# Revit family: Residential_Boiler-Lochinvar-Knight-KHB_Series
name_source: partatom
category: Mechanical Equipment
revit_build: Autodesk Revit 2014 (Build: 20130308_1515(x64)
units: mm (PartAtom-declared; Revit-internal decimal feet)

## types (12) — shared parameters
ASME Tank Construction = Yes
Assembly Code = D3020100
Default Elevation = 0"
Description = Knight Fire Tube Boiler
Drain Connection Diameter = 3/4"
Frequency = 60 Hz
Gas Connection Description = Gas Supply Connection 1/2"
Gas Supply Connection Diameter = 1/2"
Height = 43 3/8"
Hot Water Connection Diameter = 1"
I = 15"
K = 8 11/32"
Leg Width = 17"
Length = 19"
Manufacturer = Lochinvar
Material = Metal-Lochinvar-Steel
Phase = 1
Price = Prices may vary. Please consult Manufacturer Representative for most up-to-date price list.
Product Documentation Link = http://www.lochinvar.com
Product Page URL = http://www.lochinvar.com
URL = http://www.lochinvar.com
Voltage = 120 V
Warranty Information = 15-Year Limited Warranty, 5-Year Limited Parts Warranty
Width = 16"

## per-type parameters (varying)
| type | A | Air Intake Connection Description | Air Intake Connection Diameter | B | C | Cold Water Connection Description | Cold Water Connection Diameter | D | E | Exhaust Air Connection Description | Exhaust Air Connection Diameter | F | Fuel Type | G | H | Hood Width | Hot Water Connection Description | J | Shipping Weight | Total Heating Capacity | Venting Diameter |
| KHB055N | 3 1/2" | Air Intake Connection 2" | 2" | 13 1/4" | 6" | Cold Water Connection Inlet 1" NPT | 1" | 2 3/4" | 37 21/32" | Exhaust Air Connection 2" | 2" | 13 1/2" | Natural Gas | 8 11/32" | 10 1/2" | 3 1/2" | Hot Water Connection Outlet 1" NPT | 32 1/2" | 160 lb | 55000.0 Btu/h | 2" |
| KHB085N | 3 1/2" | Air Intake Connection 2" | 2" | 13 1/4" | 6" | Cold Water Connection Inlet 1" NPT | 1" | 2 3/4" | 37 21/32" | Exhaust Air Connection 2" | 2" | 13 1/2" | Natural Gas | 8 11/32" | 10 1/2" | 3 1/2" | Hot Water Connection Outlet 1" NPT | 32 1/2" | 170 lb | 85000.0 Btu/h | 2" |
| KHB110N | 2 3/4" | Air Intake Connection 3" | 3" | 14 3/4" | 7 1/2" | Cold Water Connection Inlet 1" NPT | 1" | 2 3/4" | 38" | Exhaust Air Connection 3" | 3" | 14 11/32" | Natural Gas | 9 3/4" | 10 1/2" | 2 3/4" | Hot Water Connection Outlet 1" NPT | 33" | 170 lb | 110000.0 Btu/h | 3" |
| KHB155N | 2 3/4" | Air Intake Connection 3" | 3" | 14 3/4" | 7 1/2" | Cold Water Connection Inlet 1" NPT | 1" | 2 1/2" | 38" | Exhaust Air Connection 3" | 3" | 14 11/32" | Natural Gas | 9 3/4" | 10 1/2" | 2 3/4" | Hot Water Connection Outlet 1" NPT | 33" | 180 lb | 155000.0 Btu/h | 3" |
| KHB199N | 3" | Air Intake Connection 3" | 3" | 15 1/2" | 7 1/2" | Cold Water Connection Inlet 1-1/4" NPT | 1 1/4" | 2 1/2" | 38 11/32" | Exhaust Air Connection 3" | 3" | 14 11/32" | Natural Gas | 10 1/2" | 11 1/2" | 3" | Hot Water Connection Outlet 1-1/4" NPT | 33" | 200 lb | 199999.0 Btu/h | 3" |
| KHB285N | 3" | Air Intake Connection 3" | 3" | 15 1/2" | 7 1/2" | Cold Water Connection Inlet 1-1/4" NPT | 1 1/4" | 2 1/2" | 38 11/32" | Exhaust Air Connection 3" | 3" | 14 11/32" | Natural Gas | 10 1/2" | 11 1/2" | 3" | Hot Water Connection Outlet 1-1/4" NPT | 33" | 210 lb | 285000.0 Btu/h | 3" |
| KHB285L | 3" | Air Intake Connection 3" | 3" | 15 1/2" | 7 1/2" | Cold Water Connection Inlet 1-1/4" NPT | 1 1/4" | 2 1/2" | 38 11/32" | Exhaust Air Connection 3" | 3" | 14 11/32" | LP Gas | 10 1/2" | 11 1/2" | 3" | Hot Water Connection Outlet 1-1/4" NPT | 33" | 210 lb | 285000.0 Btu/h | 3" |
| KHB055L | 3 1/2" | Air Intake Connection 2" | 2" | 13 1/4" | 6" | Cold Water Connection Inlet 1" NPT | 1" | 2 3/4" | 37 21/32" | Exhaust Air Connection 2" | 2" | 13 1/2" | LP Gas | 8 11/32" | 10 1/2" | 3 1/2" | Hot Water Connection Outlet 1" NPT | 32 1/2" | 160 lb | 55000.0 Btu/h | 2" |
| KHB085L | 3 1/2" | Air Intake Connection 2" | 2" | 13 1/4" | 6" | Cold Water Connection Inlet 1" NPT | 1" | 2 3/4" | 37 21/32" | Exhaust Air Connection 2" | 2" | 13 1/2" | LP Gas | 8 11/32" | 10 1/2" | 3 1/2" | Hot Water Connection Outlet 1" NPT | 32 1/2" | 170 lb | 85000.0 Btu/h | 2" |
| KHB110L | 2 3/4" | Air Intake Connection 3" | 3" | 14 3/4" | 7 1/2" | Cold Water Connection Inlet 1" NPT | 1" | 2 3/4" | 38" | Exhaust Air Connection 3" | 3" | 14 11/32" | LP Gas | 9 3/4" | 10 1/2" | 2 3/4" | Hot Water Connection Outlet 1" NPT | 33" | 170 lb | 110000.0 Btu/h | 3" |
| KHB155L | 2 3/4" | Air Intake Connection 3" | 3" | 14 3/4" | 7 1/2" | Cold Water Connection Inlet 1" NPT | 1" | 2 1/2" | 38" | Exhaust Air Connection 3" | 3" | 14 11/32" | LP Gas | 9 3/4" | 10 1/2" | 2 3/4" | Hot Water Connection Outlet 1" NPT | 33" | 180 lb | 155000.0 Btu/h | 3" |
| KHB199L | 3" | Air Intake Connection 3" | 3" | 15 1/2" | 7 1/2" | Cold Water Connection Inlet 1-1/4" NPT | 1 1/4" | 2 1/2" | 38 11/32" | Exhaust Air Connection 3" | 3" | 14 11/32" | LP Gas | 10 1/2" | 11 1/2" | 3" | Hot Water Connection Outlet 1-1/4" NPT | 33" | 200 lb | 199999.0 Btu/h | 3" |

note: column(s) folded — value = type name in every type: Model

## geometry (parser evidence)
native form markers: Sweep x4
no freeform markers — native parametric forms only
